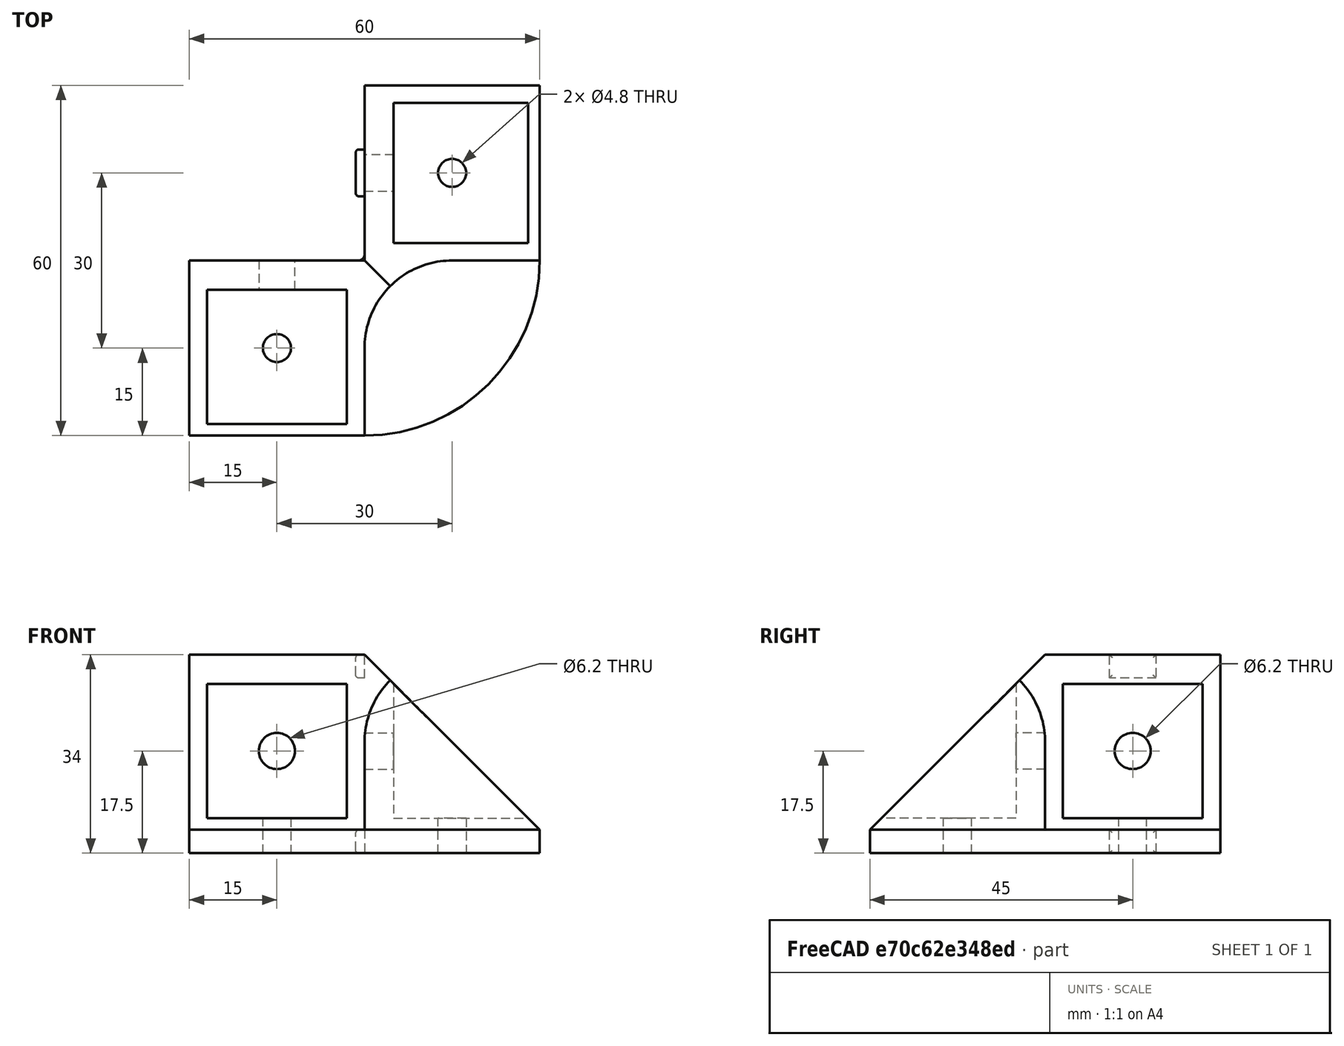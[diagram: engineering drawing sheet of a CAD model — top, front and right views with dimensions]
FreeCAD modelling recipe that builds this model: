
FCSTD DOCUMENT  (FreeCAD 1.0R39285 (Git))
Label: ShelfCorner
License: All rights reserved
objects: Sketcher::SketchObject×12, PartDesign::Pad×7, PartDesign::Pocket×5, PartDesign::Fillet×1, PartDesign::Body×1
note: 64 computed .brp shape members not serialized (recipe doc carries the construction recipe); baked Part::Feature solids carry a one-line shape summary decoded from their .brp

FEATURE [Sketcher::SketchObject] Sketch
  ArcFitTolerance = 1e-06
  AttachmentSupport = -> [XY_Plane]
  FullyConstrained = true
  MakeInternals = false
  MapMode = 5
  sketch-geometry (7):
    g0: LineSegment StartX=30 StartY=0 StartZ=0 EndX=30 EndY=-30 EndZ=0
    g1: LineSegment StartX=30 StartY=-30 StartZ=0 EndX=0 EndY=-30 EndZ=0
    g2: LineSegment StartX=0 StartY=-30 StartZ=0 EndX=0 EndY=-60 EndZ=0
    g3: LineSegment StartX=30 StartY=0 StartZ=0 EndX=60 EndY=0 EndZ=0
    g4: LineSegment StartX=0 StartY=-60 StartZ=0 EndX=30 EndY=-60 EndZ=0
    g5: LineSegment StartX=60 StartY=0 StartZ=0 EndX=60 EndY=-30 EndZ=0
    g6: ArcOfCircle CenterX=30 CenterY=-30 CenterZ=0 NormalX=0 NormalY=0 NormalZ=1 AngleXU=0 Radius=30 StartAngle=4.71239 EndAngle=6.28319
  constraints (21):
    c: PointOnObject(g0,g-1)
    c: Vertical(g0)
    c: Coincident(g1,g0)
    c: PointOnObject(g1,g-2)
    c: Horizontal(g1)
    c: Coincident(g2,g1)
    c: PointOnObject(g2,g-2)
    c: Coincident(g3,g0)
    c: PointOnObject(g3,g-1)
    c: Equal(g3,g2)
    c: Distance(g0,g0) = 30
    c: Coincident(g4,g2)
    c: Horizontal(g4)
    c: Coincident(g5,g3)
    c: Vertical(g5)
    c: Equal(g5,g0)
    c: Equal(g1,g4)
    c: Equal(g1,g0)
    c: Coincident(g5,g6)
    c: Equal(g2,g0)
    c: Tangent(g4,g6) = -1.5708
FEATURE [PartDesign::Pad] Pad
  Direction = (0,0,1)
  Length = 4
  Length2 = 10
  Profile = -> Sketch
  ReferenceAxis = -> Sketch [N_Axis]
  Refine = true
  Suppressed = false
  Type = 0
FEATURE [Sketcher::SketchObject] Sketch001
  ArcFitTolerance = 1e-06
  AttachmentSupport = -> [Pad]
  ExternalGeometry = -> [Pad]
  FullyConstrained = true
  MakeInternals = false
  MapMode = 5
  Placement = pos=(0,0,0) rot=(0,0.707107,0.707107;3.14159rad)
  sketch-geometry (3):
    g0: LineSegment StartX=-60 StartY=4 StartZ=0 EndX=-30 EndY=4 EndZ=0
    g1: LineSegment StartX=-30 StartY=4 StartZ=0 EndX=-30 EndY=34 EndZ=0
    g2: LineSegment StartX=-30 StartY=34 StartZ=0 EndX=-60 EndY=4 EndZ=0
  constraints (7):
    c: Coincident(g0,g-3)
    c: Coincident(g0,g-3)
    c: Coincident(g1,g0)
    c: Vertical(g1)
    c: Coincident(g2,g1)
    c: Coincident(g2,g0)
    c: Equal(g1,g0)
FEATURE [PartDesign::Pad] Pad001
  BaseFeature = -> Pad
  Direction = (0,1,-2e-16)
  Length = 30
  Length2 = 10
  Profile = -> Sketch001
  ReferenceAxis = -> Sketch001 [N_Axis]
  Refine = true
  Reversed = true
  Suppressed = false
  Type = 0
FEATURE [Sketcher::SketchObject] Sketch002
  ArcFitTolerance = 1e-06
  AttachmentSupport = -> [Pad001]
  ExternalGeometry = -> [Pad001]
  FullyConstrained = true
  MakeInternals = false
  MapMode = 5
  Placement = pos=(0,0,0) rot=(0.57735,-0.57735,-0.57735;2.0944rad)
  sketch-geometry (3):
    g0: LineSegment StartX=60 StartY=4 StartZ=0 EndX=30 EndY=4 EndZ=0
    g1: LineSegment StartX=30 StartY=4 StartZ=0 EndX=30 EndY=34 EndZ=0
    g2: LineSegment StartX=30 StartY=34 StartZ=0 EndX=60 EndY=4 EndZ=0
  constraints (6):
    c: Coincident(g0,g-3)
    c: Coincident(g0,g-3)
    c: Coincident(g1,g0)
    c: Coincident(g1,g-4)
    c: Coincident(g2,g1)
    c: Coincident(g2,g0)
FEATURE [PartDesign::Pad] Pad002
  BaseFeature = -> Pad001
  Direction = (-1,0,0)
  Length = 30
  Length2 = 10
  Profile = -> Sketch002
  ReferenceAxis = -> Sketch002 [N_Axis]
  Refine = true
  Reversed = true
  Suppressed = false
  Type = 0
FEATURE [Sketcher::SketchObject] Sketch003
  ArcFitTolerance = 1e-06
  AttachmentSupport = -> [Pad002]
  ExternalGeometry = -> [Pad002]
  FullyConstrained = false
  MakeInternals = false
  MapMode = 5
  Placement = pos=(0,-30,0) rot=(1,0,0;1.5708rad)
  sketch-geometry (3):
    g0: LineSegment StartX=35 StartY=37.6042 StartZ=0 EndX=35 EndY=6 EndZ=0
    g1: LineSegment StartX=35 StartY=6 StartZ=0 EndX=66.6042 EndY=6 EndZ=0
    g2: LineSegment StartX=35 StartY=37.6042 StartZ=0 EndX=66.6042 EndY=6 EndZ=0
  constraints (8):
    c: Vertical(g0)
    c: Coincident(g1,g0)
    c: Horizontal(g1)
    c: Coincident(g2,g0)
    c: Coincident(g2,g1)
    c: Equal(g0,g1)
    c: Distance(g-5,g1) = 2
    c: Distance(g-4,g0) = 5
FEATURE [PartDesign::Pocket] Pocket
  BaseFeature = -> Pad002
  Direction = (0,1,-2e-16)
  Length = 27
  Length2 = -3
  Profile = -> Sketch003
  ReferenceAxis = -> Sketch003 [N_Axis]
  Refine = true
  Suppressed = false
  Type = 4
FEATURE [Sketcher::SketchObject] Sketch004
  ArcFitTolerance = 1e-06
  AttachmentSupport = -> [Pocket]
  ExternalGeometry = -> [Pocket]
  FullyConstrained = true
  MakeInternals = false
  MapMode = 5
  Placement = pos=(30,0,0) rot=(0.57735,0.57735,0.57735;2.0944rad)
  sketch-geometry (3):
    g0: LineSegment StartX=-35 StartY=36 StartZ=0 EndX=-35 EndY=6 EndZ=0
    g1: LineSegment StartX=-35 StartY=6 StartZ=0 EndX=-65 EndY=6 EndZ=0
    g2: LineSegment StartX=-65 StartY=6 StartZ=0 EndX=-35 EndY=36 EndZ=0
  constraints (9):
    c: Vertical(g0)
    c: Coincident(g1,g0)
    c: Horizontal(g1)
    c: Coincident(g2,g1)
    c: Coincident(g2,g0)
    c: Equal(g0,g1)
    c: Distance(g0,g-4) = 5
    c: Distance(g-5,g1) = 2
    c: Equal(g0,g-4)
FEATURE [PartDesign::Pocket] Pocket001
  BaseFeature = -> Pocket
  Direction = (-1,0,0)
  Length = 27
  Length2 = -3
  Profile = -> Sketch004
  ReferenceAxis = -> Sketch004 [N_Axis]
  Refine = true
  Suppressed = false
  Type = 4
FEATURE [Sketcher::SketchObject] Sketch005
  ArcFitTolerance = 1e-06
  AttachmentSupport = -> [Pocket001]
  ExternalGeometry = -> [Pocket001]
  FullyConstrained = true
  MakeInternals = false
  MapMode = 5
  Placement = pos=(35,0,0) rot=(0.57735,0.57735,0.57735;2.0944rad)
  sketch-geometry (1):
    g0: Circle CenterX=-15 CenterY=17.5 CenterZ=0 NormalX=0 NormalY=0 NormalZ=1 AngleXU=0 Radius=3.1
  constraints (2):
    c: Symmetric(g-5,g-6,g0)
    c: Diameter(g0) = 6.2
FEATURE [PartDesign::Pocket] Pocket002
  BaseFeature = -> Pocket001
  Direction = (-1,0,0)
  Length = 5
  Length2 = 5
  Profile = -> Sketch005
  ReferenceAxis = -> Sketch005 [N_Axis]
  Refine = true
  Suppressed = false
  Type = 1
FEATURE [Sketcher::SketchObject] Sketch006
  ArcFitTolerance = 1e-06
  AttachmentSupport = -> [Pocket002]
  ExternalGeometry = -> [Pocket002]
  FullyConstrained = true
  MakeInternals = false
  MapMode = 5
  Placement = pos=(0,-35,0) rot=(1,0,0;1.5708rad)
  sketch-geometry (1):
    g0: Circle CenterX=15 CenterY=17.5 CenterZ=0 NormalX=0 NormalY=0 NormalZ=1 AngleXU=0 Radius=3.1
  constraints (2):
    c: Symmetric(g-3,g-4,g0)
    c: Diameter(g0) = 6.2
FEATURE [PartDesign::Pocket] Pocket003
  BaseFeature = -> Pocket002
  Direction = (0,1,-2e-16)
  Length = 5
  Length2 = 5
  Profile = -> Sketch006
  ReferenceAxis = -> Sketch006 [N_Axis]
  Refine = true
  Suppressed = false
  Type = 1
FEATURE [Sketcher::SketchObject] Sketch007
  ArcFitTolerance = 1e-06
  AttachmentSupport = -> [Pocket003]
  ExternalGeometry = -> [Pocket003]
  FullyConstrained = true
  MakeInternals = false
  MapMode = 5
  Placement = pos=(0,0,6) rot=(0,0,1;0rad)
  sketch-geometry (4):
    g0: Circle CenterX=15 CenterY=-45 CenterZ=0 NormalX=0 NormalY=0 NormalZ=1 AngleXU=0 Radius=2.4
    g1: Circle CenterX=45 CenterY=-15 CenterZ=0 NormalX=0 NormalY=0 NormalZ=1 AngleXU=0 Radius=2.4
    g2: LineSegment [constr] StartX=15 StartY=-45 StartZ=0 EndX=15 EndY=-30 EndZ=0
    g3: LineSegment [constr] StartX=45 StartY=-15 StartZ=0 EndX=30 EndY=-15 EndZ=0
  constraints (10):
    c: Equal(g1,g0)
    c: Diameter(g0) = 4.8
    c: Distance(g0,g-3) = 15
    c: Distance(g1,g-4) = 15
    c: Coincident(g2,g0)
    c: Symmetric(g-3,g-3,g2)
    c: Vertical(g2)
    c: Coincident(g3,g1)
    c: Symmetric(g-4,g-4,g3)
    c: Horizontal(g3)
FEATURE [PartDesign::Pocket] Pocket004
  BaseFeature = -> Pocket003
  Direction = (0,0,-1)
  Length = 5
  Length2 = 5
  Profile = -> Sketch007
  ReferenceAxis = -> Sketch007 [N_Axis]
  Refine = true
  Suppressed = false
  Type = 1
FEATURE [Sketcher::SketchObject] Sketch008
  ArcFitTolerance = 1e-06
  AttachmentSupport = -> [Pocket004]
  ExternalGeometry = -> [Pocket004]
  FullyConstrained = true
  MakeInternals = false
  MapMode = 5
  Placement = pos=(0,0,0) rot=(1,0,0;3.14159rad)
  sketch-geometry (3):
    g0: ArcOfCircle CenterX=29 CenterY=29 CenterZ=0 NormalX=0 NormalY=0 NormalZ=1 AngleXU=0 Radius=1 StartAngle=7e-16 EndAngle=1.5708
    g1: LineSegment StartX=29 StartY=30 StartZ=0 EndX=30 EndY=30 EndZ=0
    g2: LineSegment StartX=30 StartY=30 StartZ=0 EndX=30 EndY=29 EndZ=0
  constraints (7):
    c: Tangent(g0,g-3) = -1.5708
    c: Tangent(g0,g-4) = -1.5708
    c: Radius(g0) = 1
    c: Coincident(g1,g0)
    c: Coincident(g1,g-4)
    c: Coincident(g2,g1)
    c: Coincident(g2,g0)
FEATURE [PartDesign::Pad] Pad003
  BaseFeature = -> Pocket004
  Direction = (0,0,-1)
  Length = 34
  Length2 = 10
  Profile = -> Sketch008
  ReferenceAxis = -> Sketch008 [N_Axis]
  Refine = true
  Reversed = true
  Suppressed = false
  Type = 0
FEATURE [Sketcher::SketchObject] Sketch009
  ArcFitTolerance = 1e-06
  AttachmentSupport = -> [Pad003]
  ExternalGeometry = -> [Pad003]
  FullyConstrained = true
  MakeInternals = false
  MapMode = 5
  Placement = pos=(0,0,4) rot=(0,0,1;0rad)
  sketch-geometry (3):
    g0: LineSegment StartX=30 StartY=-30 StartZ=0 EndX=34.3934 EndY=-34.3934 EndZ=0
    g1: ArcOfCircle CenterX=45 CenterY=-45 CenterZ=0 NormalX=0 NormalY=0 NormalZ=1 AngleXU=0 Radius=15 StartAngle=2.35619 EndAngle=3.14159
    g2: LineSegment StartX=30 StartY=-30 StartZ=0 EndX=30 EndY=-45 EndZ=0
  constraints (8):
    c: Coincident(g0,g-4)
    c: Perpendicular(g1,g0)
    c: Tangent(g1,g-4) = -1.5708
    c: Coincident(g1,g0)
    c: Angle(g-4,g0) = 0.785398
    c: Coincident(g2,g0)
    c: Coincident(g2,g1)
    c: Radius(g1) = 15
FEATURE [PartDesign::Pad] Pad004
  BaseFeature = -> Pad003
  Direction = (0,0,1)
  Length = 10
  Length2 = 10
  Profile = -> Sketch009
  ReferenceAxis = -> Sketch009 [N_Axis]
  Refine = true
  Suppressed = false
  Type = 3
  UpToFace = -> Pad003 [Face8]
FEATURE [Sketcher::SketchObject] Sketch010
  ArcFitTolerance = 1e-06
  AttachmentSupport = -> [Pad004]
  ExternalGeometry = -> [Pad004]
  FullyConstrained = true
  MakeInternals = false
  MapMode = 5
  Placement = pos=(0,0,4) rot=(0,0,1;0rad)
  sketch-geometry (3):
    g0: LineSegment StartX=30 StartY=-30 StartZ=0 EndX=34.3934 EndY=-34.3934 EndZ=0
    g1: ArcOfCircle CenterX=45 CenterY=-45 CenterZ=0 NormalX=0 NormalY=0 NormalZ=1 AngleXU=0 Radius=15 StartAngle=1.5708 EndAngle=2.35619
    g2: LineSegment StartX=30 StartY=-30 StartZ=0 EndX=45 EndY=-30 EndZ=0
  constraints (7):
    c: Coincident(g0,g-4)
    c: Coincident(g0,g-3)
    c: Coincident(g1,g0)
    c: Tangent(g1,g-4) = 1.5708
    c: Radius(g1) = 15
    c: Coincident(g2,g0)
    c: Tangent(g2,g1) = 1.5708
FEATURE [PartDesign::Pad] Pad005
  BaseFeature = -> Pad004
  Direction = (0,0,1)
  Length = 10
  Length2 = 10
  Profile = -> Sketch010
  ReferenceAxis = -> Sketch010 [N_Axis]
  Refine = true
  Suppressed = false
  Type = 3
  UpToFace = -> Pad004 [Face20]
FEATURE [Sketcher::SketchObject] Sketch011
  ArcFitTolerance = 1e-06
  AttachmentSupport = -> [Pad005]
  ExternalGeometry = -> [Pad005]
  FullyConstrained = true
  MakeInternals = false
  MapMode = 5
  Placement = pos=(30,0,0) rot=(0.57735,-0.57735,-0.57735;2.0944rad)
  sketch-geometry (12):
    g0: LineSegment StartX=11 StartY=34 StartZ=0 EndX=11 EndY=30 EndZ=0
    g1: LineSegment StartX=11 StartY=30 StartZ=0 EndX=19 EndY=30 EndZ=0
    g2: LineSegment StartX=19 StartY=30 StartZ=0 EndX=19 EndY=34 EndZ=0
    g3: LineSegment StartX=19 StartY=34 StartZ=0 EndX=11 EndY=34 EndZ=0
    g4: LineSegment StartX=11 StartY=4 StartZ=0 EndX=11 EndY=0 EndZ=0
    g5: LineSegment StartX=11 StartY=0 StartZ=0 EndX=19 EndY=0 EndZ=0
    g6: LineSegment StartX=19 StartY=0 StartZ=0 EndX=19 EndY=4 EndZ=0
    g7: LineSegment StartX=19 StartY=4 StartZ=0 EndX=11 EndY=4 EndZ=0
    g8: LineSegment [constr] StartX=-7.5e-15 StartY=34 StartZ=0 EndX=30 EndY=34 EndZ=0
    g9: LineSegment [constr] StartX=0 StartY=0 StartZ=0 EndX=30 EndY=0 EndZ=0
    g10: LineSegment [constr] StartX=15 StartY=0 StartZ=0 EndX=15 EndY=4 EndZ=0
    g11: LineSegment [constr] StartX=15 StartY=34 StartZ=0 EndX=15 EndY=30 EndZ=0
  constraints (31):
    c: Coincident(g0,g1)
    c: Coincident(g1,g2)
    c: Coincident(g2,g3)
    c: Coincident(g3,g0)
    c: Vertical(g0)
    c: Vertical(g2)
    c: Horizontal(g1)
    c: Coincident(g4,g5)
    c: Coincident(g5,g6)
    c: Coincident(g6,g7)
    c: Coincident(g7,g4)
    c: Vertical(g4)
    c: Horizontal(g5)
    c: Horizontal(g7)
    c: PointOnObject(g5,g-1)
    c: Equal(g7,g1)
    c: DistanceX(g3,g3) = 8
    c: Coincident(g8,g-3)
    c: Coincident(g8,g-4)
    c: Coincident(g9,g-1)
    c: Coincident(g9,g-4)
    c: Symmetric(g5,g5,g10)
    c: Symmetric(g7,g7,g10)
    c: Symmetric(g0,g2,g11)
    c: PointOnObject(g11,g3)
    c: PointOnObject(g11,g1)
    c: Equal(g10,g11)
    c: DistanceY(g11,g11) = 4
    c: PointOnObject(g0,g8)
    c: Symmetric(g8,g8,g11)
    c: Symmetric(g9,g9,g10)
FEATURE [PartDesign::Pad] Pad006
  BaseFeature = -> Pad005
  Direction = (-1,0,0)
  Length = 1.5
  Length2 = 10
  Profile = -> Sketch011
  ReferenceAxis = -> Sketch011 [N_Axis]
  Refine = true
  Suppressed = false
  Type = 0
FEATURE [PartDesign::Fillet] Fillet
  Base = -> Pad006 [Face35,Face26]
  BaseFeature = -> Pad006
  Radius = 0.5
  Refine = true
  SupportTransform = false
  Suppressed = false
  UseAllEdges = false
FEATURE [PartDesign::Body] Body
  AllowCompound = false
  Group = -> [Sketch,Pad,Sketch001,Pad001,Sketch002,Pad002,Sketch003,Pocket,Sketch004,Pocket001,Sketch005,Pocket002,Sketch006,Pocket003,Sketch007,Pocket004,Sketch008,Pad003,Sketch009,Pad004,Sketch010,Pad005,Sketch011,Pad006,Fillet]
  Origin = -> Origin
  Tip = -> Fillet
